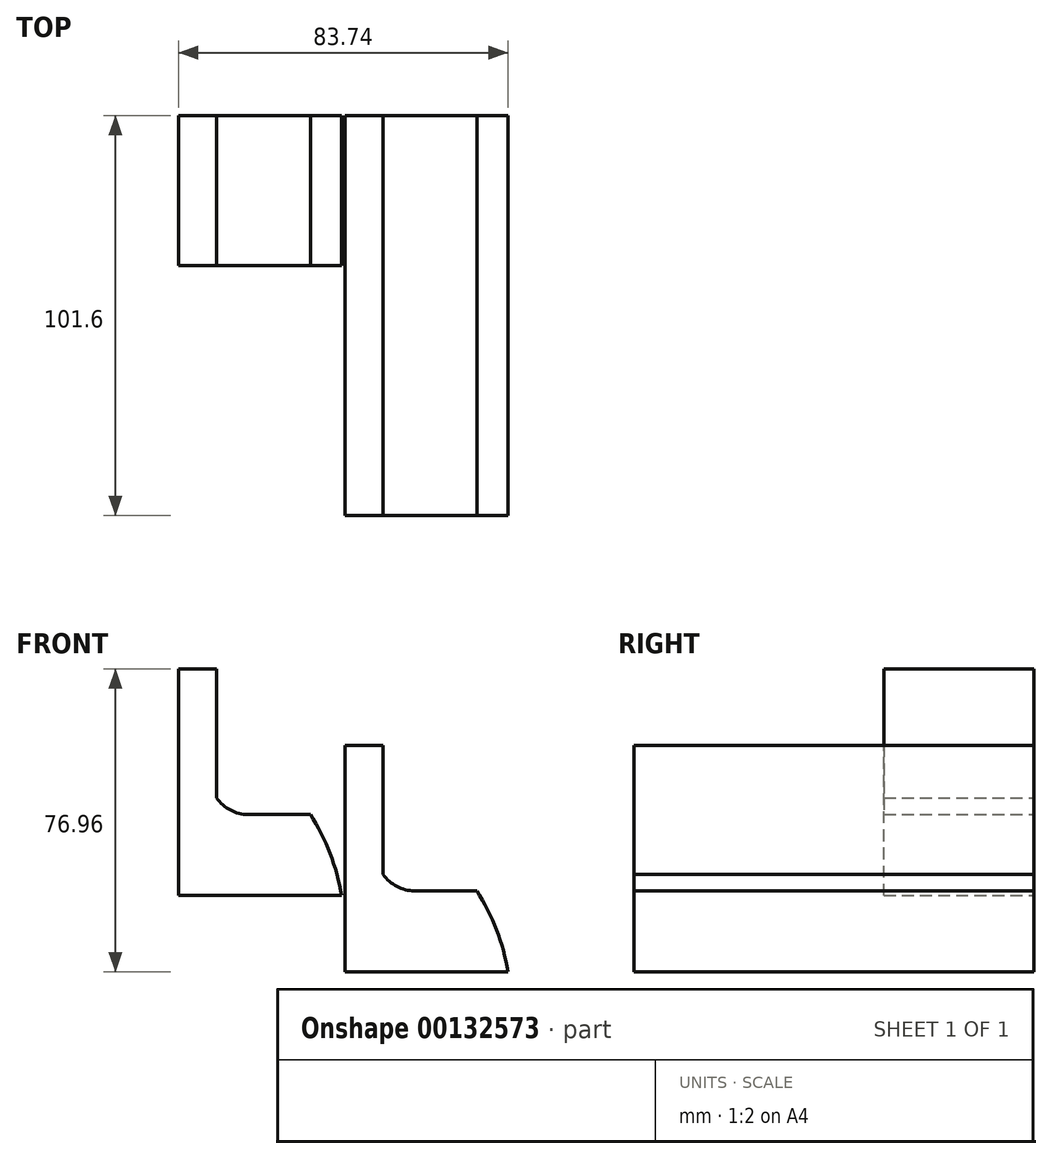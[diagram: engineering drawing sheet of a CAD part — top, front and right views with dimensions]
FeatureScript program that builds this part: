
annotation { "Feature Type Name" : "Feature", "Feature Type Description" : "" }
export const myFeature = defineFeature(function(context is Context, id is Id, definition is map)
    precondition{}
    {
        {
            var Q0;
            Q0=qCreatedBy(makeId("Front.planeOp"),FACE);
            var sketch = newSketch(context, id + "F0", { "sketchPlane" : qUnion([Q0])});
            skLineSegment(sketch, "E0", {"start": v(-49.64, 51.23) * mm, "end": v(-49.64, 18.46) * mm});
            skLineSegment(sketch, "E1", {"start": v(-41.72, 14.26) * mm, "end": v(-25.88, 14.26) * mm});
            skLineSegment(sketch, "E2", {"start": v(-25.88, -6.34) * mm, "end": v(-59.41, -6.34) * mm});
            skLineSegment(sketch, "E3", {"start": v(-59.41, -6.34) * mm, "end": v(-59.41, 51.23) * mm});
            skLineSegment(sketch, "E4", {"start": v(-59.41, 51.23) * mm, "end": v(-49.64, 51.23) * mm});
            skArc(sketch, "E5", {"start": v(-17.96, -6.34) * mm, "mid": v(-20.87, 4.36) * mm, "end": v(-25.88, 14.26) * mm});
            skLineSegment(sketch, "E6", {"start": v(-25.88, -6.34) * mm, "end": v(-17.96, -6.34) * mm});
            skArc(sketch, "E7", {"start": v(-49.64, 18.46) * mm, "mid": v(-46.2, 15.37) * mm, "end": v(-41.72, 14.26) * mm});
            skArc(sketch, "E8", {"start": v(-49.64, 51.23) * mm, "mid": v(-52.3, 44.5) * mm, "end": v(-49.64, 37.76) * mm});
            skSolve(sketch);
        }
        {
            var Q0;
            Q0 = qSketchRegion(id + "F0", true);
            extrude(context, id + "F1", {"entities" : qUnion([Q0]), "depth" : 38.1 * mm});
        }
        {
            var Q0;
            Q0=qCreatedBy(makeId("Front.planeOp"),FACE);
            var sketch = newSketch(context, id + "F2", { "sketchPlane" : qUnion([Q0])});
            skLineSegment(sketch, "E9", {"start": v(-7.36, 31.84) * mm, "end": v(-7.36, -0.93) * mm});
            skLineSegment(sketch, "E10", {"start": v(0.57, -5.13) * mm, "end": v(16.4, -5.13) * mm});
            skLineSegment(sketch, "E11", {"start": v(16.4, -25.73) * mm, "end": v(-17.13, -25.73) * mm});
            skLineSegment(sketch, "E12", {"start": v(-17.13, -25.73) * mm, "end": v(-17.13, 31.84) * mm});
            skLineSegment(sketch, "E13", {"start": v(-17.13, 31.84) * mm, "end": v(-7.36, 31.84) * mm});
            skArc(sketch, "E14", {"start": v(24.33, -25.73) * mm, "mid": v(21.42, -15.03) * mm, "end": v(16.4, -5.13) * mm});
            skLineSegment(sketch, "E15", {"start": v(16.4, -25.73) * mm, "end": v(24.33, -25.73) * mm});
            skArc(sketch, "E16", {"start": v(-7.36, -0.93) * mm, "mid": v(-3.92, -4.02) * mm, "end": v(0.57, -5.13) * mm});
            skArc(sketch, "E17", {"start": v(-7.36, 31.84) * mm, "mid": v(-10, 25.1) * mm, "end": v(-7.36, 18.37) * mm});
            skSolve(sketch);
        }
        {
            var Q0;
            Q0 = qSketchRegion(id + "F2", true);
            extrude(context, id + "F3", {"entities" : qUnion([Q0]), "depth" : 101.6 * mm});
        }
    });
